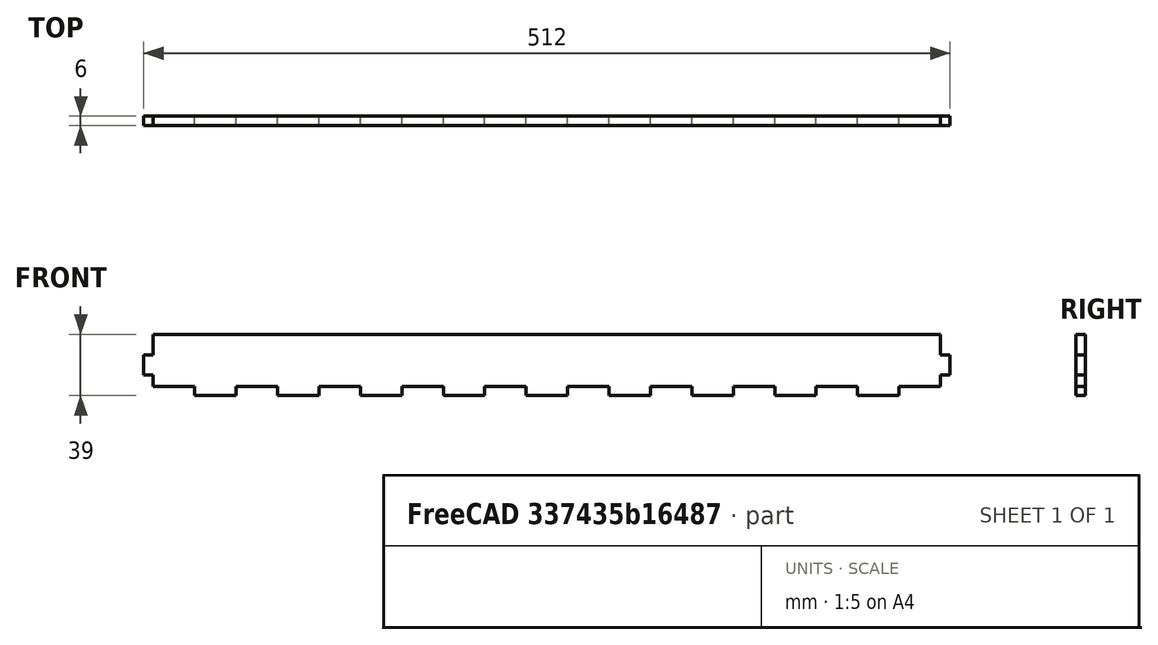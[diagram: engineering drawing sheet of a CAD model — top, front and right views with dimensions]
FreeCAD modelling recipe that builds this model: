
FCSTD DOCUMENT  (FreeCAD 0.16R6527 (Git))
Label: side_333
License: All rights reserved
LicenseURL: http://en.wikipedia.org/wiki/All_rights_reserved
objects: Part::Box×3, Part::FeaturePython×2, Part::Cut×2
note: 7 computed .brp shape members not serialized (recipe doc carries the construction recipe); baked Part::Feature solids carry a one-line shape summary decoded from their .brp

FEATURE [Part::Box] Box  label="Strip"
  Height = 39
  Length = 512
  Width = 6
  expr: Height = side_500#Strip.Height
  expr: Width = bottom#Slab.Height
  expr: Length = bottom#Slab.Width
FEATURE [Part::Box] Box001  label="Horizontal_hole"
  Height = 6
  Length = 26.3158
  Width = 10
  expr: Height = bottom#Vertical_hole.Length
  expr: Length = bottom#Vertical_hole.Width
FEATURE [Part::FeaturePython] Array001  label="Horizontal_Array"  # Draft array (typed FeaturePython)
  Angle = 360
  ArrayType = 0
  Axis = (0,0,1)
  Base = -> Box001
  Center = (0,0,0)
  Fuse = false
  IntervalAxis = (0,0,0)
  IntervalX = (52.6316,0,0)
  IntervalY = (0,1,0)
  IntervalZ = (0,0,0)
  NumberPolar = 1
  NumberX = 10
  NumberY = 1
  NumberZ = 1
  Placement = pos=(6,0,0) rot=(0,0,1;0rad)
  expr: Placement.Base.x = bottom#Slab.Height
  expr: IntervalX.x = Horizontal_hole.Length * 2
FEATURE [Part::Box] Box002  label="Vertical_Hole"
  Height = 13
  Length = 6
  Width = 10
  expr: Height = side_500#Vertical_Hole.Height
  expr: Length = Strip.Width
FEATURE [Part::FeaturePython] Array003  label="Vertical_Array"  # Draft array (typed FeaturePython)
  Angle = 360
  ArrayType = 0
  Axis = (0,0,1)
  Base = -> Box002
  Center = (0,0,0)
  Fuse = false
  IntervalAxis = (0,0,0)
  IntervalX = (506,0,0)
  IntervalY = (0,1,0)
  IntervalZ = (0,0,26)
  NumberPolar = 1
  NumberX = 2
  NumberY = 1
  NumberZ = 2
  expr: IntervalX.x = Strip.Length - Strip.Width
  expr: IntervalZ.z = Vertical_Hole.Height * 2
FEATURE [Part::Cut] Cut  label="Horizontal_Cut"
  Base = -> Box
  Tool = -> Array001
FEATURE [Part::Cut] Cut001
  Base = -> Cut
  Tool = -> Array003
